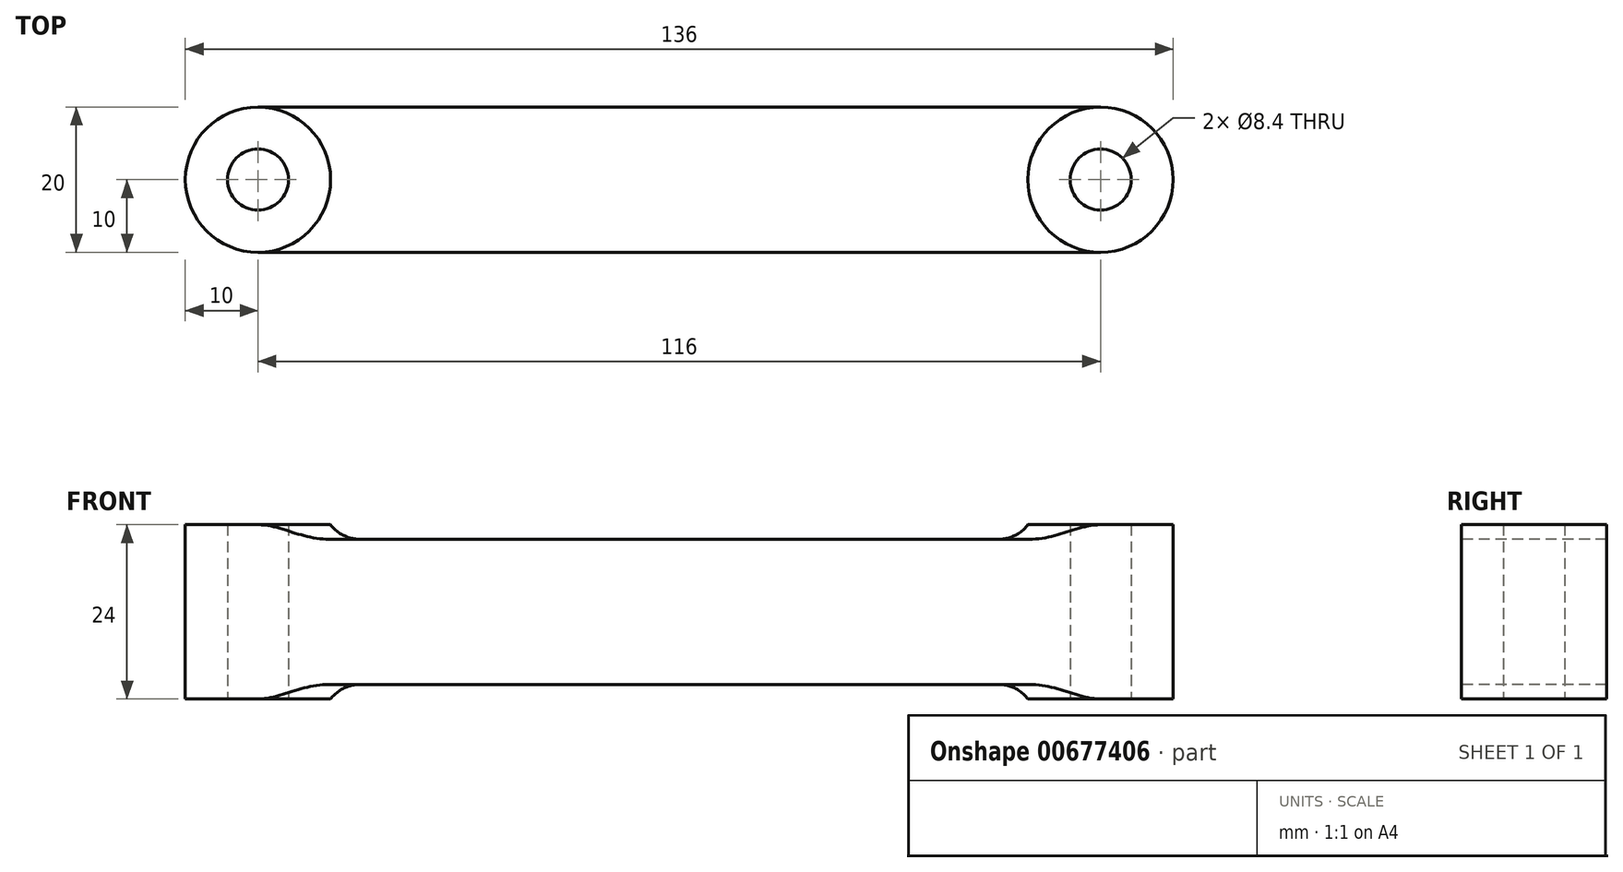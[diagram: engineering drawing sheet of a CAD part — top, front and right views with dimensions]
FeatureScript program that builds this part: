
annotation { "Feature Type Name" : "Feature", "Feature Type Description" : "" }
export const myFeature = defineFeature(function(context is Context, id is Id, definition is map)
    precondition{}
    {
        {
            var Q0;
            Q0=qCreatedBy(makeId("Top.planeOp"),FACE);
            var sketch = newSketch(context, id + "F0", { "sketchPlane" : qUnion([Q0])});
            skLineSegment(sketch, "E0.bottom", {"start": v(58, -10) * mm, "end": v(-58, -10) * mm});
            skLineSegment(sketch, "E0.top", {"start": v(58, 10) * mm, "end": v(-58, 10) * mm});
            skPoint(sketch, "E0.middle", {"position": v(0, 0) * mm});
            skCircle(sketch, "E1", {"center": v(-58, 0) * mm, "radius": 4.2 * mm});
            skPoint(sketch, "E1.centerSnap0", {"position": v(-68, 0) * mm});
            skCircle(sketch, "E2", {"center": v(58, 0) * mm, "radius": 4.2 * mm});
            skPoint(sketch, "E2.centerSnap0", {"position": v(68, 0) * mm});
            skArc(sketch, "E3", {"start": v(-58, 10) * mm, "mid": v(-68, 0) * mm, "end": v(-58, -10) * mm});
            skArc(sketch, "E4", {"start": v(58, -10) * mm, "mid": v(68, 0) * mm, "end": v(58, 10) * mm});
            skSolve(sketch);
        }
        {
            var Q0;
            Q0=makeQuery(id+"F0.imprint","IMPRINT",FACE,{"disambiguationData":[TD([[makeQuery(id+"F0.imprint","IMPRINT",EDGE,{"derivedFrom":sQuery(id+"F0.wireOp",EDGE,"E0.bottom")}),-1.0]])]});
            extrude(context, id + "F1", {"entities" : qUnion([Q0]), "depth" : 20 * mm, "offsetDistance" : 25 * mm});
        }
        {
            var Q0;
            Q0=makeQuery(id+"F1.opExtrude","CAP_FACE",FACE,{"disambiguationData":[OSD([sQuery(id+"F0.wireOp",EDGE,"E0.bottom"),sQuery(id+"F0.wireOp",EDGE,"E0.top"),sQuery(id+"F0.wireOp",EDGE,"E1"),sQuery(id+"F0.wireOp",EDGE,"E2"),sQuery(id+"F0.wireOp",EDGE,"E3"),sQuery(id+"F0.wireOp",EDGE,"E4")])],"isStart":false});
            var sketch = newSketch(context, id + "F2", { "sketchPlane" : qUnion([Q0])});
            skCircle(sketch, "E5", {"center": v(-58, 0) * mm, "radius": 10 * mm});
            skCircle(sketch, "E6", {"center": v(58, 0) * mm, "radius": 10 * mm});
            skCircle(sketch, "E7.0", {"center": v(-58, 0) * mm, "radius": 4.2 * mm});
            skCircle(sketch, "E8.0", {"center": v(58, 0) * mm, "radius": 4.2 * mm});
            skSolve(sketch);
        }
        {
            var Q0;
            Q0=qSketchRegion(id+"F2",true);
            extrude(context, id + "F3", {"entities" : qUnion([Q0]), "operationType" : NewBodyOperationType.ADD, "depth" : 2 * mm, "offsetDistance" : 25 * mm, "hasSecondDirection" : true, "secondDirectionOppositeDirection" : true, "secondDirectionDepth" : 22 * mm});
        }
        {
            var Q0;
            Q0=makeQuery(id+"F3.boolean.opBoolean","INTERSECT",EDGE,{"derivedFrom":[makeQuery(id+"F1.opExtrude","CAP_FACE",FACE,{"disambiguationData":[OSD([sQuery(id+"F0.wireOp",EDGE,"E0.bottom"),sQuery(id+"F0.wireOp",EDGE,"E0.top"),sQuery(id+"F0.wireOp",EDGE,"E1"),sQuery(id+"F0.wireOp",EDGE,"E2"),sQuery(id+"F0.wireOp",EDGE,"E3"),sQuery(id+"F0.wireOp",EDGE,"E4")])],"isStart":false}),makeQuery(id+"F3.opExtrude","SWEPT_FACE",FACE,{"disambiguationData":[OSD([sQuery(id+"F2.wireOp",EDGE,"E5")])]})]});
            var Q1;
            Q1=makeQuery(id+"F3.boolean.opBoolean","INTERSECT",EDGE,{"derivedFrom":[makeQuery(id+"F1.opExtrude","CAP_FACE",FACE,{"disambiguationData":[OSD([sQuery(id+"F0.wireOp",EDGE,"E0.bottom"),sQuery(id+"F0.wireOp",EDGE,"E0.top"),sQuery(id+"F0.wireOp",EDGE,"E1"),sQuery(id+"F0.wireOp",EDGE,"E2"),sQuery(id+"F0.wireOp",EDGE,"E3"),sQuery(id+"F0.wireOp",EDGE,"E4")])],"isStart":true}),makeQuery(id+"F3.opExtrude","SWEPT_FACE",FACE,{"disambiguationData":[OSD([sQuery(id+"F2.wireOp",EDGE,"E5")])]})]});
            var Q2;
            Q2=makeQuery(id+"F3.boolean.opBoolean","INTERSECT",EDGE,{"derivedFrom":[makeQuery(id+"F1.opExtrude","CAP_FACE",FACE,{"disambiguationData":[OSD([sQuery(id+"F0.wireOp",EDGE,"E0.bottom"),sQuery(id+"F0.wireOp",EDGE,"E0.top"),sQuery(id+"F0.wireOp",EDGE,"E1"),sQuery(id+"F0.wireOp",EDGE,"E2"),sQuery(id+"F0.wireOp",EDGE,"E3"),sQuery(id+"F0.wireOp",EDGE,"E4")])],"isStart":true}),makeQuery(id+"F3.opExtrude","SWEPT_FACE",FACE,{"disambiguationData":[OSD([sQuery(id+"F2.wireOp",EDGE,"E6")])]})]});
            var Q3;
            Q3=makeQuery(id+"F3.boolean.opBoolean","INTERSECT",EDGE,{"derivedFrom":[makeQuery(id+"F1.opExtrude","CAP_FACE",FACE,{"disambiguationData":[OSD([sQuery(id+"F0.wireOp",EDGE,"E0.bottom"),sQuery(id+"F0.wireOp",EDGE,"E0.top"),sQuery(id+"F0.wireOp",EDGE,"E1"),sQuery(id+"F0.wireOp",EDGE,"E2"),sQuery(id+"F0.wireOp",EDGE,"E3"),sQuery(id+"F0.wireOp",EDGE,"E4")])],"isStart":false}),makeQuery(id+"F3.opExtrude","SWEPT_FACE",FACE,{"disambiguationData":[OSD([sQuery(id+"F2.wireOp",EDGE,"E6")])]})]});
            fillet(context, id + "F4", {"entities" : qUnion([Q0, Q1, Q2, Q3]), "radius" : 5 * mm, "tangentPropagation" : true, "allowEdgeOverflow" : false});
        }
    });
